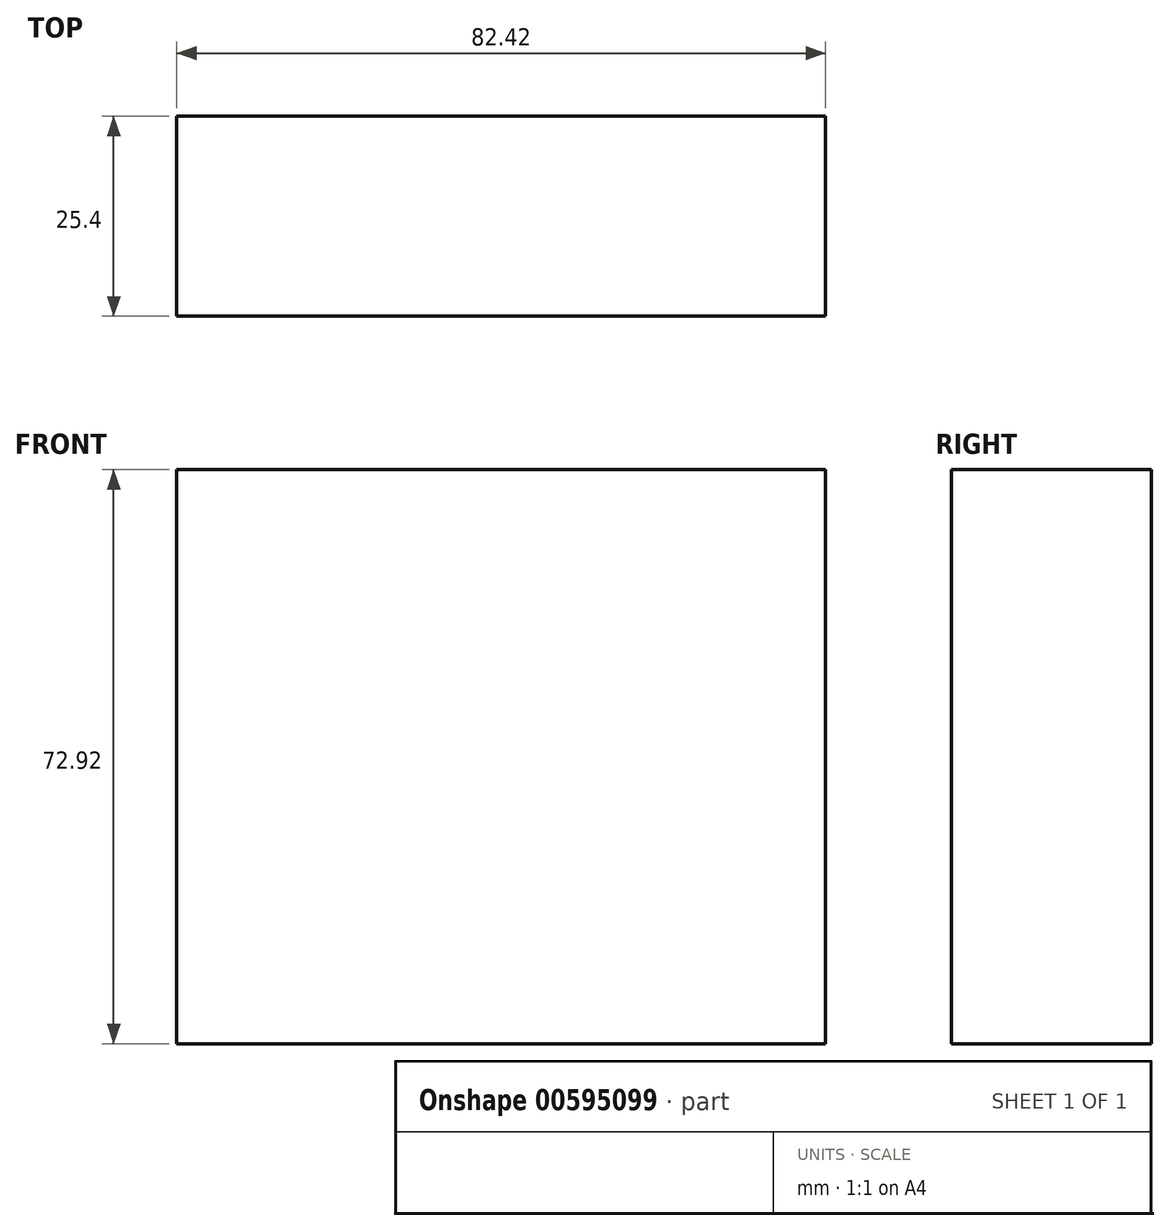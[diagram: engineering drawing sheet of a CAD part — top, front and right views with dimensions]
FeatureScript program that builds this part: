
annotation { "Feature Type Name" : "Feature", "Feature Type Description" : "" }
export const myFeature = defineFeature(function(context is Context, id is Id, definition is map)
    precondition{}
    {
        {
            var Q0;
            Q0=qCreatedBy(makeId("Front.planeOp"),FACE);
            var sketch = newSketch(context, id + "F0", { "sketchPlane" : qUnion([Q0])});
            skLineSegment(sketch, "E0.bottom", {"start": v(41.21, 36.46) * mm, "end": v(-41.21, 36.46) * mm});
            skLineSegment(sketch, "E0.top", {"start": v(41.21, -36.46) * mm, "end": v(-41.21, -36.46) * mm});
            skLineSegment(sketch, "E0.left", {"start": v(41.21, 36.46) * mm, "end": v(41.21, -36.46) * mm});
            skLineSegment(sketch, "E0.right", {"start": v(-41.21, 36.46) * mm, "end": v(-41.21, -36.46) * mm});
            skPoint(sketch, "E0.middle", {"position": v(0, 0) * mm});
            skSolve(sketch);
        }
        {
            var Q0;
            Q0 = qSketchRegion(id + "F0", true);
            extrude(context, id + "F1", {"entities" : qUnion([Q0]), "depth" : 25.4 * mm, "offsetDistance" : 25.4 * mm});
        }
    });
